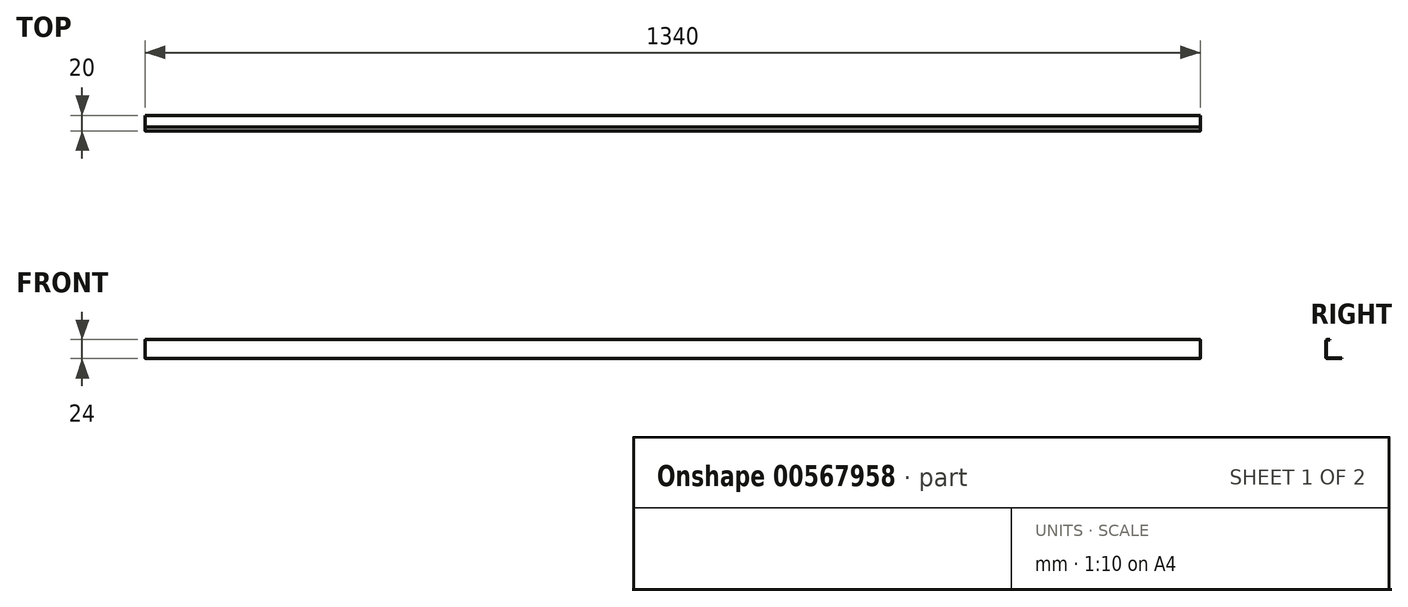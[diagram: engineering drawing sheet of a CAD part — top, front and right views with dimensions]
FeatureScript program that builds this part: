
annotation { "Feature Type Name" : "Feature", "Feature Type Description" : "" }
export const myFeature = defineFeature(function(context is Context, id is Id, definition is map)
    precondition{}
    {
        {
            var Q0;
            Q0=qCreatedBy(makeId("Right.planeOp"),FACE);
            var sketch = newSketch(context, id + "F0", { "sketchPlane" : qUnion([Q0])});
            skLineSegment(sketch, "E0", {"start": v(10, -12) * mm, "end": v(-9, -12) * mm});
            skArc(sketch, "E1", {"start": v(-9, -12) * mm, "mid": v(-9.7, -11.7) * mm, "end": v(-10, -11) * mm});
            skLineSegment(sketch, "E2", {"start": v(-10, -11) * mm, "end": v(-10, 11) * mm});
            skArc(sketch, "E3", {"start": v(-10, 11) * mm, "mid": v(-9.7, 11.7) * mm, "end": v(-9, 12) * mm});
            skLineSegment(sketch, "E4", {"start": v(-9, 12) * mm, "end": v(-5, 12) * mm});
            skLineSegment(sketch, "E5", {"start": v(-5, 12) * mm, "end": v(-5, 11.5) * mm});
            skLineSegment(sketch, "E6", {"start": v(-5, 11.5) * mm, "end": v(-9, 11.5) * mm});
            skArc(sketch, "E7", {"start": v(-9, 11.5) * mm, "mid": v(-9.35, 11.35) * mm, "end": v(-9.5, 11) * mm});
            skLineSegment(sketch, "E8", {"start": v(-9.5, 11) * mm, "end": v(-9.5, -11) * mm});
            skArc(sketch, "E9", {"start": v(-9.5, -11) * mm, "mid": v(-9.35, -11.35) * mm, "end": v(-9, -11.5) * mm});
            skLineSegment(sketch, "E10", {"start": v(-9, -11.5) * mm, "end": v(10, -11.5) * mm});
            skLineSegment(sketch, "E11", {"start": v(10, -11.5) * mm, "end": v(10, -12) * mm});
            skSolve(sketch);
        }
        {
            var Q0;
            Q0 = qSketchRegion(id + "F0", true);
            extrude(context, id + "F1", {"entities" : qUnion([Q0]), "oppositeDirection" : true, "depth" : 1340 * mm, "offsetDistance" : 25 * mm});
        }
    });
